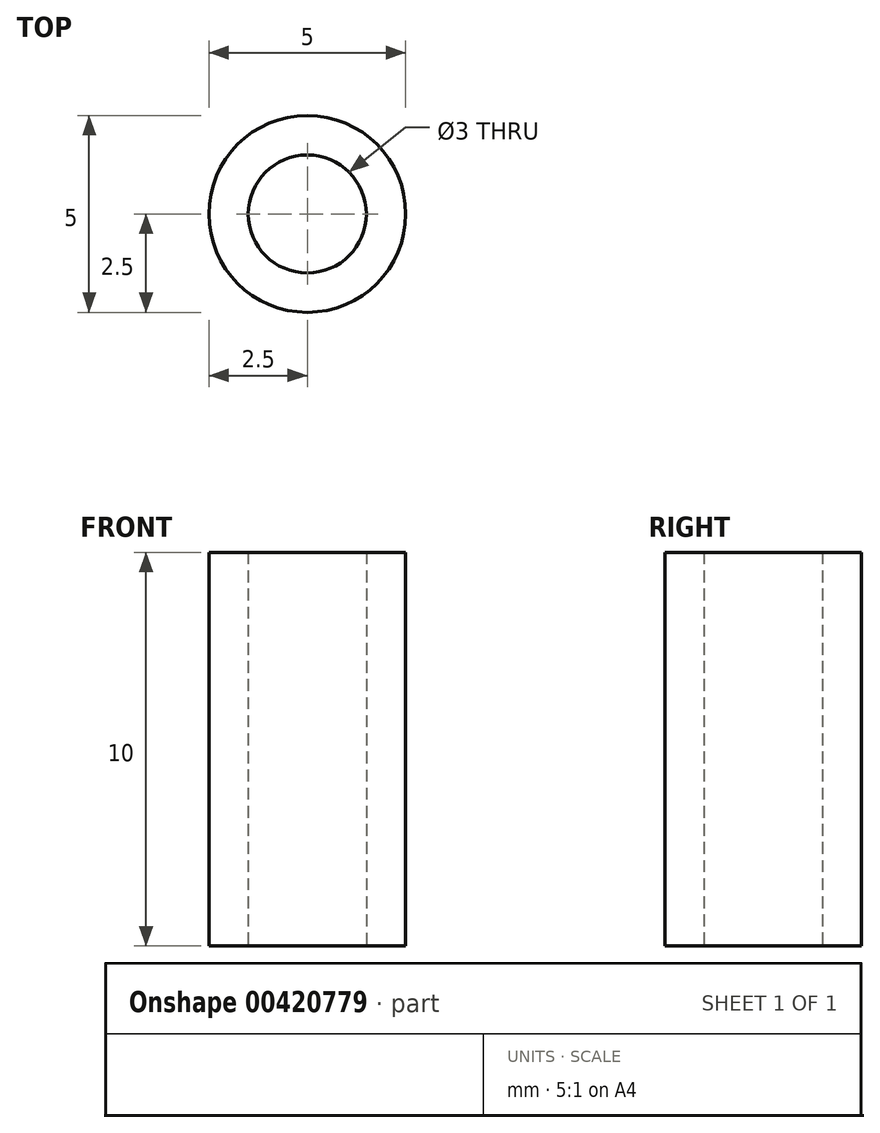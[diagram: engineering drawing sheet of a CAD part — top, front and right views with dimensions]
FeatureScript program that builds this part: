
annotation { "Feature Type Name" : "Feature", "Feature Type Description" : "" }
export const myFeature = defineFeature(function(context is Context, id is Id, definition is map)
    precondition{}
    {
        {
            var Q0;
            Q0=qCreatedBy(makeId("Top.planeOp"),FACE);
            var sketch = newSketch(context, id + "F0", { "sketchPlane" : qUnion([Q0])});
            skCircle(sketch, "E0", {"center": v(0, 0) * mm, "radius": 2.5 * mm});
            skCircle(sketch, "E1", {"center": v(0, 0) * mm, "radius": 1.5 * mm});
            skSolve(sketch);
        }
        {
            var Q0;
            Q0=makeQuery(id+"F0.imprint","IMPRINT",FACE,{"disambiguationData":[TD([[makeQuery(id+"F0.imprint","IMPRINT",EDGE,{"derivedFrom":sQuery(id+"F0.wireOp",EDGE,"E0")}),1.0]])]});
            extrude(context, id + "F1", {"entities" : qUnion([Q0]), "depth" : 10 * mm});
        }
    });
